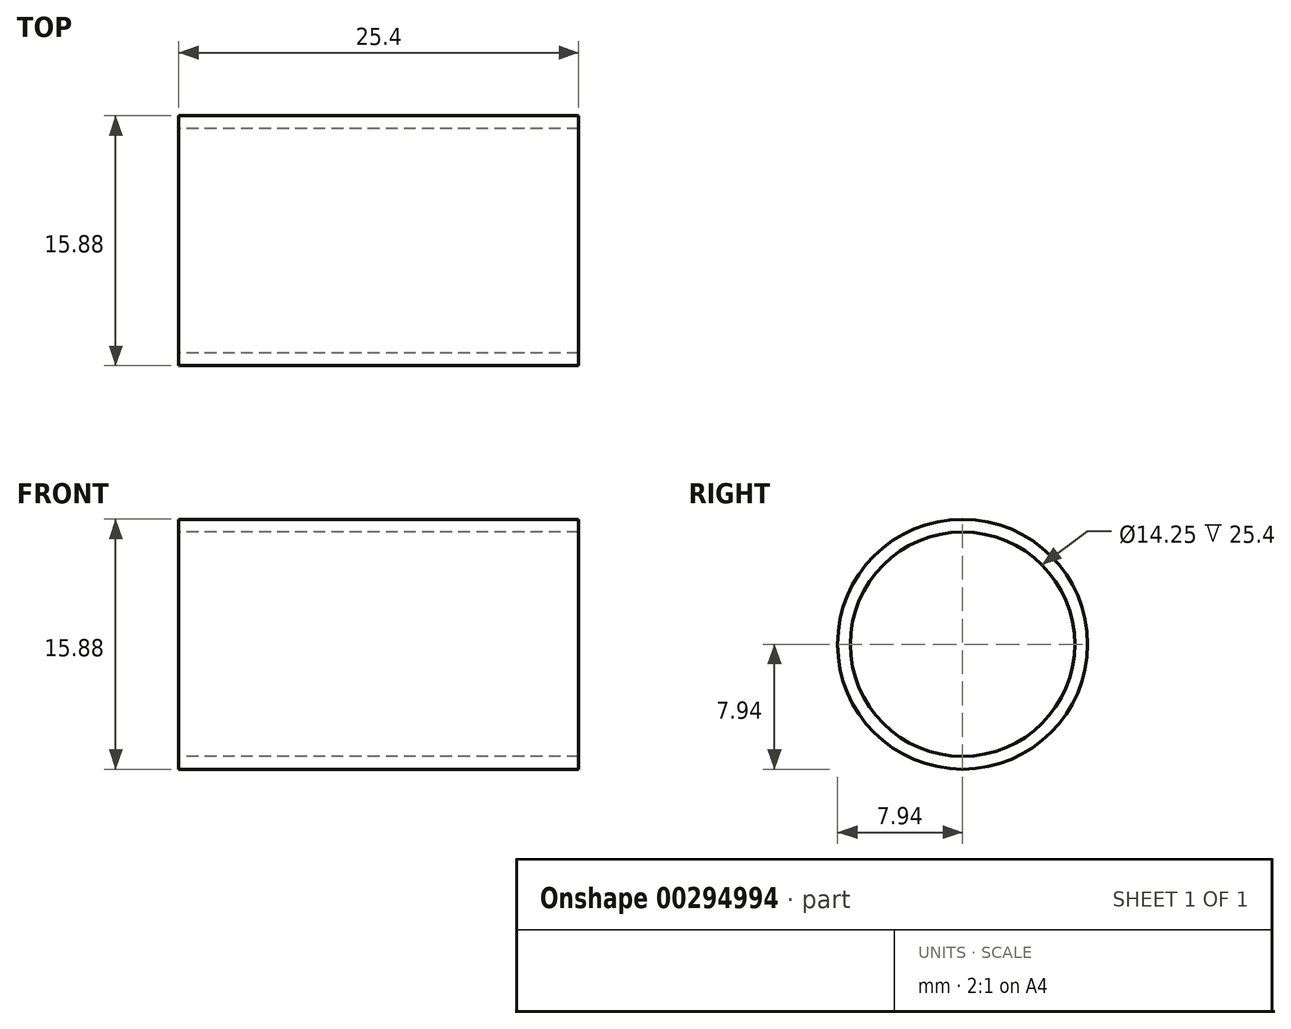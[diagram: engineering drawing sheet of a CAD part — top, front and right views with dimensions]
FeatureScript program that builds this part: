
annotation { "Feature Type Name" : "Feature", "Feature Type Description" : "" }
export const myFeature = defineFeature(function(context is Context, id is Id, definition is map)
    precondition{}
    {
        {
            var Q0;
            Q0=qCreatedBy(makeId("Right.planeOp"),FACE);
            var sketch = newSketch(context, id + "F0", { "sketchPlane" : qUnion([Q0])});
            skCircle(sketch, "E0", {"center": v(0, 0) * mm, "radius": 7.94 * mm});
            skCircle(sketch, "E1", {"center": v(0, 0) * mm, "radius": 7.12 * mm});
            skSolve(sketch);
        }
        {
            var Q0;
            Q0 = qSketchRegion(id + "F0", true);
            extrude(context, id + "F1", {"entities" : qUnion([Q0]), "depth" : 25.4 * mm});
        }
    });
